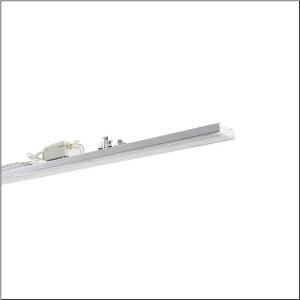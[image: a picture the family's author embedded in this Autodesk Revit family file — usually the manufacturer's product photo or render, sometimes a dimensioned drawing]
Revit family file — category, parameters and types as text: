
# Revit family: licross_r__21_recessed_mo_52te19dn495g_53e3
name_source: partatom
category: Lighting Fixtures
units: mm (PartAtom-declared; Revit-internal decimal feet)

## family parameters
Cut with Voids When Loaded = No
Host = Face
Light Source = No
Part Type = Normal
Room Calculation Point = No
Round Connector Dimension = Use Diameter
Shared = No

## types (1)
- --- (1 x LED, 9850 lm, 58 W, 4000K)
    Apparent Load = 58 VA
    CIE Flux Codes = 55 90 98 100 100
    Color Rendering = 80
    Color Temperature = 4000K
    Default Elevation = 1800 mm
    Description = Licross® 21 Recessed MO, luminaire insert, of sheet steel, galvanised, coil coated, white, length: 1.500mm, width: 66mm, height: 67mm, LED rated luminous flux: 9.850lm, light colour: 840, control gear: DALI 2, with plug, 5-pole, with phase selection, mains connection: 220..240V, AC, 50/60Hz, rated input power: 58W, halogen-free wiring, primary light control with lens, of plastic, primary optical cover: cover, of PMMA, light emission: direct distribution, primary light characteristic: double asymmetric, protection rating (complete): IP54, insulation class (complete): insulation class I (protective earthing), certification: CE, ENEC, VDE, UKCA, protection symbol: D if used in an environment with non-conductive dust loads with corresponding accessories, impact resistance: IK06, permissible ambient temperature for indoor applications: -25..+35°C, corresponds to IFS (International Featured Standards) requirements for safety and quality in the food industry, reducing of maximum allowable ambient temperature of 5°C with ceiling mounting, LABS conformity tested according to VDMA 24364:2018-05, packaging unit: 1 piece
    Height = 58 mm
    Lamp = 1 x LED
    Lamp Light Flux = 9850 lm
    Lamp Power = 58 W
    Lamp count = 1
    Length = 1500 mm
    Luminous efficacy = 170 lm/W
    Manufacturer = Siteco
    ModVariant = No
    Model = 52TE19DN495G
    Mounting Place = Ceiling
    Mounting Type = Pendant
    Number of Poles = 1
    OnlyDefault = Yes
    Power Factor = 1
    Product Name = Licross® 21 Recessed MO
    Product group = luminaire insert
    ProductGroupID = 901
    Protection Class = Protection class I
    Protection Degree = IP 54
    RLX_Detail_Level = 1
    RLX_Emergency_Light_Flux = 0 lm
    RLX_Emergency_Type = 0
    RLX_Emergency_Type_DB = No
    RlxData = <blob elided: 24545 chars, md5=c7e243bf>
    Socket = socket
    Standby Power = 0 W
    System Light Flux = 9850 lm
    System Power = 58 W
    Type Comments = factory setting: luminous flux: 100 % | dim-lin: 254 | 390 mA
    Type Image = l_1296930.jpg
    URL = http://relux.com
    VarID = @adj_059535
    Voltage = 0 V
    Weight = 0.00 kg
    Width = 66 mm

## geometry (parser evidence)
native form markers: Blend x4, Sweep x10
no freeform markers — native parametric forms only
